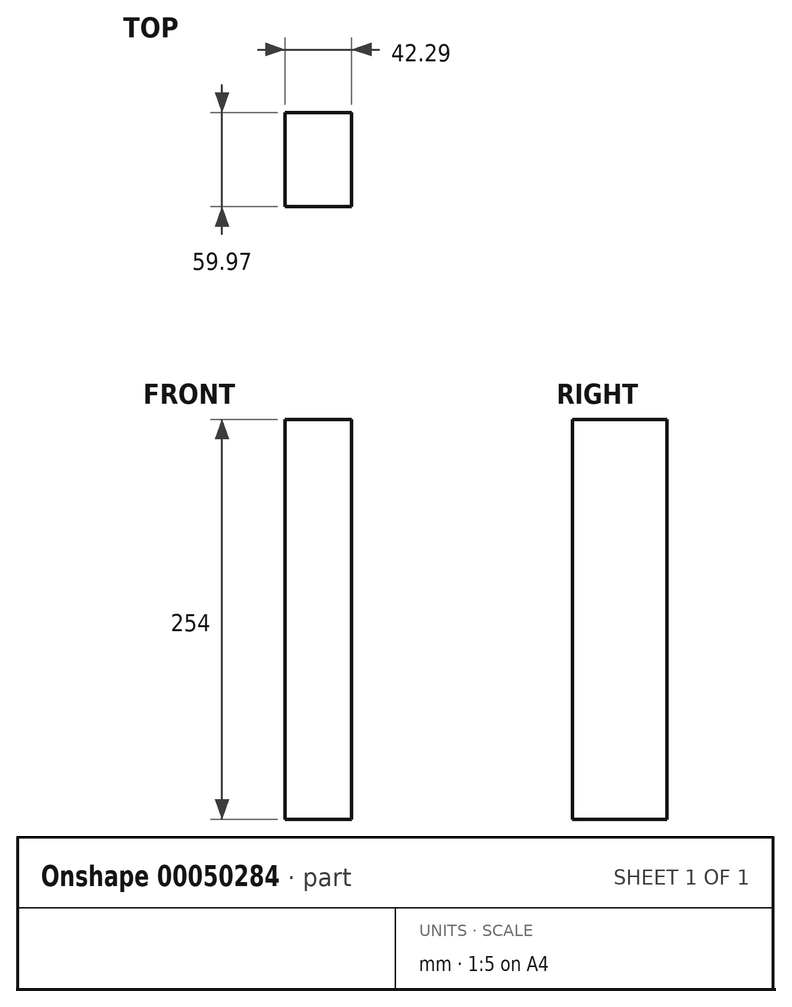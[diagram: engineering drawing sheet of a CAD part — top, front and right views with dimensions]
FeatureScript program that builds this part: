
annotation { "Feature Type Name" : "Feature", "Feature Type Description" : "" }
export const myFeature = defineFeature(function(context is Context, id is Id, definition is map)
    precondition{}
    {
        {
            var Q0;
            Q0=qCreatedBy(makeId("Top.planeOp"),FACE);
            var sketch = newSketch(context, id + "F0", { "sketchPlane" : qUnion([Q0])});
            skLineSegment(sketch, "E0.bottom", {"start": v(-36.98, -71.05) * mm, "end": v(5.31, -71.05) * mm});
            skLineSegment(sketch, "E0.top", {"start": v(-36.98, -11.08) * mm, "end": v(5.31, -11.08) * mm});
            skLineSegment(sketch, "E0.left", {"start": v(-36.98, -71.05) * mm, "end": v(-36.98, -11.08) * mm});
            skLineSegment(sketch, "E0.right", {"start": v(5.31, -71.05) * mm, "end": v(5.31, -11.08) * mm});
            skSolve(sketch);
        }
        {
            var Q0;
            Q0=makeQuery(id+"F0.imprint","IMPRINT",FACE,{"disambiguationData":[TD([[makeQuery(id+"F0.imprint","IMPRINT",EDGE,{"derivedFrom":sQuery(id+"F0.wireOp",EDGE,"E0.bottom")}),1.0]])]});
            extrude(context, id + "F1", {"entities" : qUnion([Q0]), "depth" : 254 * mm});
        }
    });
